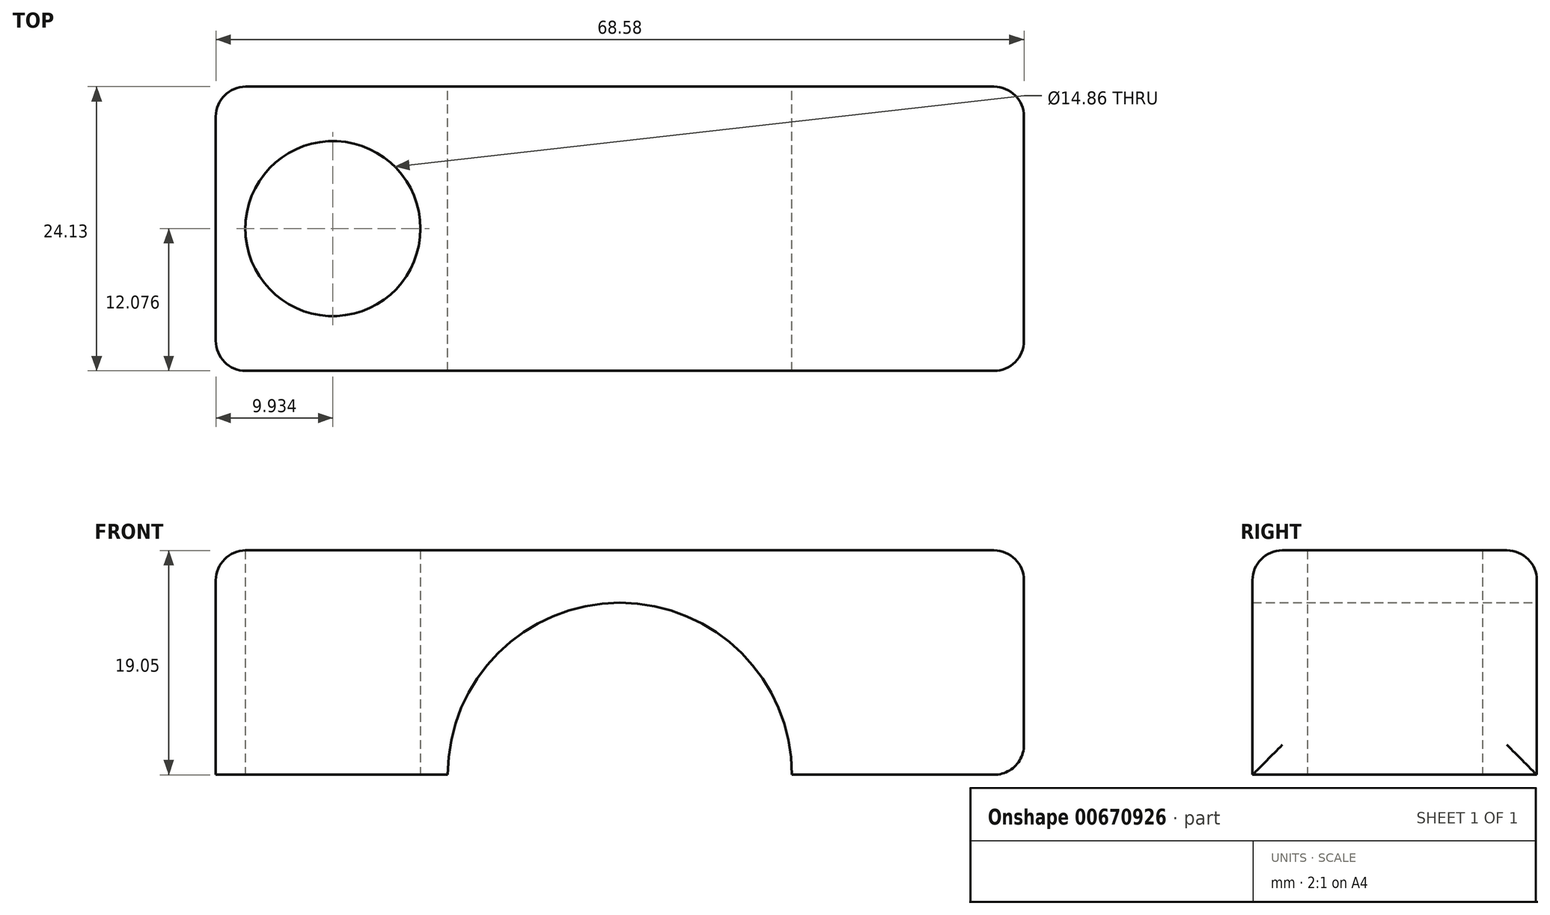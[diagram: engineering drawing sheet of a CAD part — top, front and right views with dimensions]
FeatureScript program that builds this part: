
annotation { "Feature Type Name" : "Feature", "Feature Type Description" : "" }
export const myFeature = defineFeature(function(context is Context, id is Id, definition is map)
    precondition{}
    {
        {
            var Q0;
            Q0=qCreatedBy(makeId("Front.planeOp"),FACE);
            var sketch = newSketch(context, id + "F0", { "sketchPlane" : qUnion([Q0])});
            skLineSegment(sketch, "E0.bottom", {"start": v(-7.14, 32.7) * mm, "end": v(12.54, 32.7) * mm});
            skLineSegment(sketch, "E0.top", {"start": v(-3.33, 51.75) * mm, "end": v(61.44, 51.75) * mm});
            skLineSegment(sketch, "E0.left", {"start": v(-7.14, 32.7) * mm, "end": v(-7.14, 47.94) * mm});
            skLineSegment(sketch, "E0.right", {"start": v(61.44, 32.7) * mm, "end": v(61.44, 51.75) * mm});
            skLineSegment(sketch, "E1", {"start": v(27.15, 51.75) * mm, "end": v(27.15, 47.59) * mm, "construction": true});
            skArc(sketch, "E2", {"start": v(41.75, 32.7) * mm, "mid": v(27.15, 47.3) * mm, "end": v(12.54, 32.7) * mm});
            skLineSegment(sketch, "E3.trimOffspring", {"start": v(41.75, 32.7) * mm, "end": v(61.44, 32.7) * mm});
            skLineSegment(sketch, "E4", {"start": v(-7.14, 32.7) * mm, "end": v(-7.14, 51.75) * mm});
            skLineSegment(sketch, "E5", {"start": v(61.44, 51.75) * mm, "end": v(-7.14, 51.75) * mm});
            skSolve(sketch);
        }
        {
            var Q0;
            Q0 = qSketchRegion(id + "F0", true);
            extrude(context, id + "F1", {"entities" : qUnion([Q0]), "depth" : 24.13 * mm, "offsetDistance" : 25.4 * mm});
        }
        {
            var Q0;
            Q0=qCreatedBy(makeId("Top.planeOp"),FACE);
            var sketch = newSketch(context, id + "F2", { "sketchPlane" : qUnion([Q0])});
            skLineSegment(sketch, "E6", {"start": v(-7.15, -24.12) * mm, "end": v(27.14, -24.12) * mm, "construction": true});
            skCircle(sketch, "E7", {"center": v(2.8, -12.05) * mm, "radius": 7.43 * mm});
            skCircle(sketch, "E8.MirrorC", {"center": v(51.5, -12.05) * mm, "radius": 7.43 * mm});
            skSolve(sketch);
        }
        {
            var Q0;
            Q0=makeQuery(id+"F2.imprint","IMPRINT",FACE,{"disambiguationData":[TD([[makeQuery(id+"F2.imprint","IMPRINT",EDGE,{"derivedFrom":sQuery(id+"F2.wireOp",EDGE,"E8.MirrorC")}),-1.0]])]});
            var Q1;
            Q1=makeQuery(id+"F2.imprint","IMPRINT",FACE,{"disambiguationData":[TD([[makeQuery(id+"F2.imprint","IMPRINT",EDGE,{"derivedFrom":sQuery(id+"F2.wireOp",EDGE,"E7")}),1.0]])]});
            var Q2;
            Q2=sQuery(id+"F2.wireOp",EDGE,"E7");
            var Q3;
            Q3=sQuery(id+"F2.wireOp",EDGE,"E8.MirrorC");
            extrude(context, id + "F3", {"entities" : qUnion([Q0, Q1]), "operationType" : NewBodyOperationType.REMOVE, "surfaceEntities" : qUnion([Q2, Q3]), "depth" : 54.6 * mm, "offsetDistance" : 25.4 * mm});
        }
        {
            var Q0;
            Q0=makeQuery(id+"F1.opExtrude","CAP_EDGE",EDGE,{"disambiguationData":[OSD([sQuery(id+"F0.wireOp",EDGE,"E0.right")])],"isStart":true});
            var Q1;
            Q1=makeQuery(id+"F1.opExtrude","CAP_EDGE",EDGE,{"disambiguationData":[OSD([sQuery(id+"F0.wireOp",EDGE,"E4")])],"isStart":true});
            var Q2;
            Q2=makeQuery(id+"F1.opExtrude","CAP_EDGE",EDGE,{"disambiguationData":[OSD([sQuery(id+"F0.wireOp",EDGE,"E4")])],"isStart":false});
            var Q3;
            Q3=makeQuery(id+"F1.opExtrude","CAP_EDGE",EDGE,{"disambiguationData":[OSD([sQuery(id+"F0.wireOp",EDGE,"E5")])],"isStart":false});
            var Q4;
            Q4=makeQuery(id+"F1.opExtrude","CAP_EDGE",EDGE,{"disambiguationData":[OSD([sQuery(id+"F0.wireOp",EDGE,"E5")])],"isStart":true});
            var Q5;
            Q5=makeQuery(id+"F1.opExtrude","CAP_EDGE",EDGE,{"disambiguationData":[OSD([sQuery(id+"F0.wireOp",EDGE,"E0.right")])],"isStart":false});
            var Q6;
            Q6=makeQuery(id+"F1.opExtrude","SWEPT_EDGE",EDGE,{"disambiguationData":[OSD([sQuery(id+"F0.wireOp",EDGE,"E4"),sQuery(id+"F0.wireOp",EDGE,"E5")])]});
            var Q7;
            Q7=makeQuery(id+"F1.opExtrude","SWEPT_EDGE",EDGE,{"disambiguationData":[OSD([sQuery(id+"F0.wireOp",EDGE,"E0.right"),sQuery(id+"F0.wireOp",EDGE,"E5")])]});
            fillet(context, id + "F4", {"entities" : qUnion([Q0, Q1, Q2, Q3, Q4, Q5, Q6, Q7]), "radius" : 2.54 * mm, "tangentPropagation" : true, "allowEdgeOverflow" : false});
        }
    });
